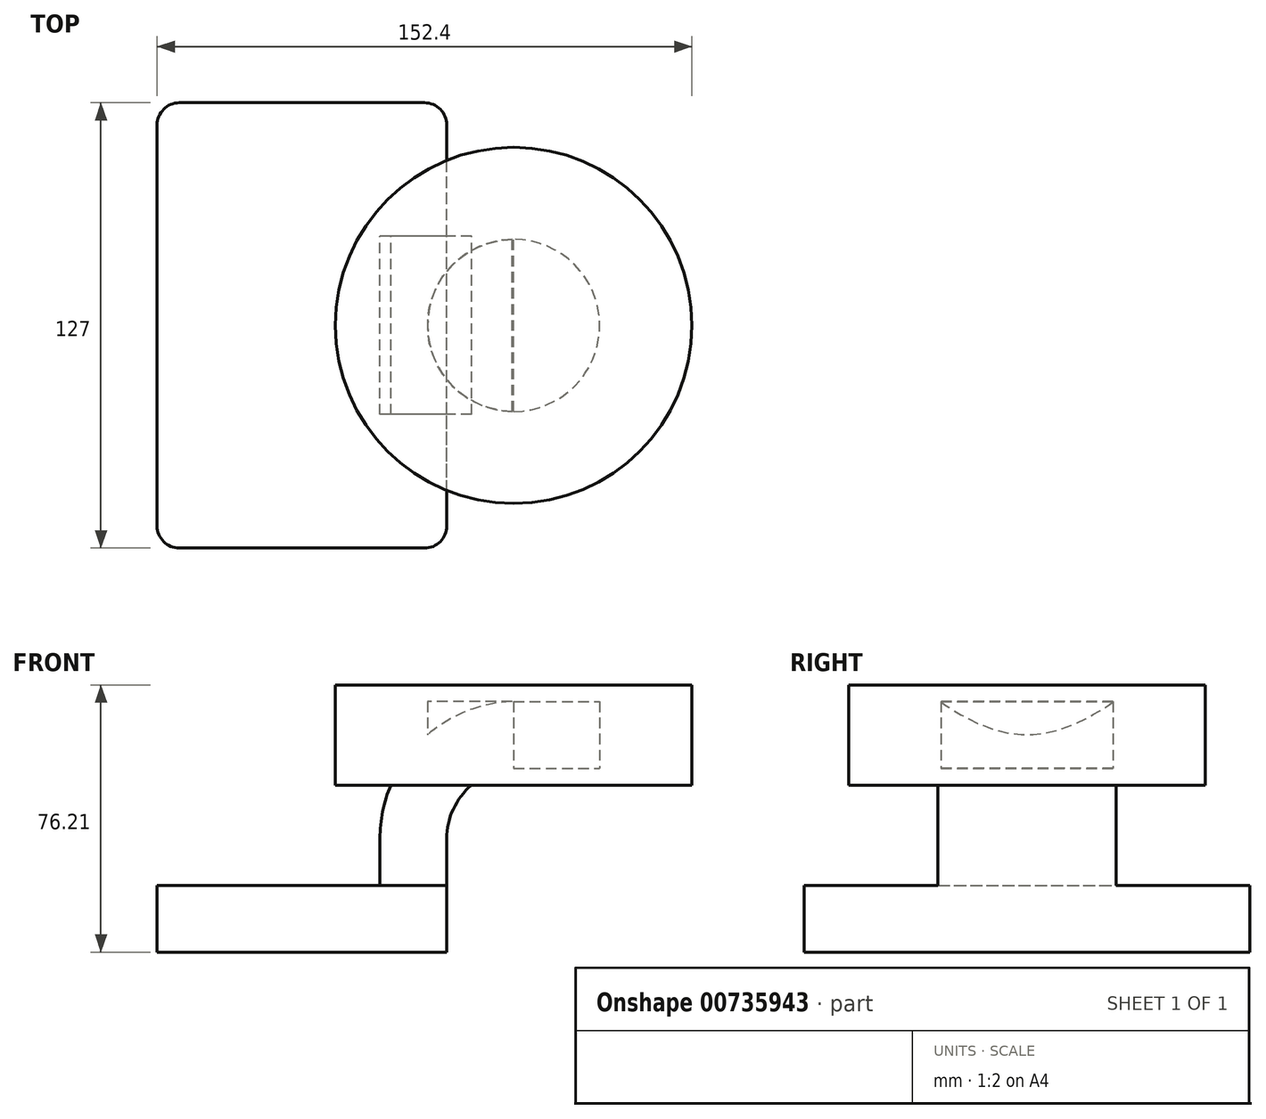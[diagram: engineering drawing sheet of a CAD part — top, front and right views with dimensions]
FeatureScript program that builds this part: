
annotation { "Feature Type Name" : "Feature", "Feature Type Description" : "" }
export const myFeature = defineFeature(function(context is Context, id is Id, definition is map)
    precondition{}
    {
        {
            var Q0;
            Q0=qCreatedBy(makeId("Front.planeOp"),FACE);
            var sketch = newSketch(context, id + "F0", { "sketchPlane" : qUnion([Q0])});
            skLineSegment(sketch, "E0.bottom", {"start": v(41.28, -9.53) * mm, "end": v(-41.28, -9.53) * mm});
            skLineSegment(sketch, "E0.top", {"start": v(41.27, 9.53) * mm, "end": v(-41.28, 9.52) * mm});
            skLineSegment(sketch, "E0.left", {"start": v(41.28, -9.53) * mm, "end": v(41.28, 9.53) * mm});
            skLineSegment(sketch, "E0.right", {"start": v(-41.28, -9.53) * mm, "end": v(-41.28, 9.52) * mm});
            skPoint(sketch, "E0.middle", {"position": v(0, 0) * mm});
            skLineSegment(sketch, "E1.bottom", {"start": v(111.13, 38.1) * mm, "end": v(60.33, 38.1) * mm});
            skLineSegment(sketch, "E1.top", {"start": v(111.13, 66.67) * mm, "end": v(60.33, 66.67) * mm});
            skLineSegment(sketch, "E1.left", {"start": v(111.13, 38.1) * mm, "end": v(111.13, 66.68) * mm});
            skLineSegment(sketch, "E1.right", {"start": v(60.33, 38.1) * mm, "end": v(60.33, 66.68) * mm});
            skPoint(sketch, "E1.middle", {"position": v(85.73, 52.39) * mm});
            skLineSegment(sketch, "E2", {"start": v(41.27, 9.53) * mm, "end": v(41.27, 22.81) * mm});
            skArc(sketch, "E3", {"start": v(41.28, 22.81) * mm, "mid": v(46.8, 36.64) * mm, "end": v(60.33, 42.88) * mm});
            skLineSegment(sketch, "E4", {"start": v(60.33, 42.88) * mm, "end": v(84.86, 42.88) * mm});
            skLineSegment(sketch, "E5.0", {"start": v(59.91, 61.93) * mm, "end": v(84.86, 61.93) * mm});
            skArc(sketch, "E5.1", {"start": v(22.23, 22.81) * mm, "mid": v(33.18, 49.97) * mm, "end": v(59.91, 61.93) * mm});
            skLineSegment(sketch, "E5.2", {"start": v(22.23, 9.53) * mm, "end": v(22.23, 22.81) * mm});
            skLineSegment(sketch, "E6", {"start": v(84.86, 42.88) * mm, "end": v(84.86, 61.93) * mm});
            skFitSpline(sketch, "E7", {"points": [v(-41.28, 9.52) * mm, v(59.91, 61.93) * mm], "startDerivative": vector(47.33, 115.64) * mm, "endDerivative": vector(112.02, -9.85) * mm});
            skSolve(sketch);
        }
        {
            var Q0;
            Q0=makeQuery(id+"F0.imprint","IMPRINT",FACE,{"disambiguationData":[TD([[makeQuery(id+"F0.imprint","IMPRINT",EDGE,{"derivedFrom":sQuery(id+"F0.wireOp",EDGE,"E0.bottom")}),-1.0]])]});
            extrude(context, id + "F1", {"entities" : qUnion([Q0]), "endBound" : BoundingType.SYMMETRIC, "depth" : 127 * mm, "offsetDistance" : 25.4 * mm});
        }
        {
            var Q0;
            {var subQ1=sQuery(id+"F0.wireOp",EDGE,"E2");Q0=makeQuery(id+"F0.imprint","IMPRINT",FACE,{"disambiguationData":[TD([[makeQuery(id+"F0.imprint","IMPRINT",EDGE,{"derivedFrom":subQ1}),1.0]])]});}
            extrude(context, id + "F2", {"entities" : qUnion([Q0]), "operationType" : NewBodyOperationType.ADD, "endBound" : BoundingType.SYMMETRIC, "depth" : 50.8 * mm, "offsetDistance" : 25.4 * mm});
        }
        {
            var Q0;
            Q0=makeQuery(id+"F0.imprint","IMPRINT",FACE,{"disambiguationData":[TD([[makeQuery(id+"F0.imprint","IMPRINT",EDGE,{"derivedFrom":sQuery(id+"F0.wireOp",EDGE,"E5.1")}),1.0]])]});
            extrude(context, id + "F3", {"entities" : qUnion([Q0]), "operationType" : NewBodyOperationType.ADD, "endBound" : BoundingType.SYMMETRIC, "depth" : 15.88 * mm, "offsetDistance" : 25.4 * mm});
        }
        {
            var Q0;
            {var subQ1=sQuery(id+"F0.wireOp",EDGE,"E1.bottom");Q0=makeQuery(id+"F0.imprint","IMPRINT",FACE,{"disambiguationData":[TD([[makeQuery(id+"F0.imprint","IMPRINT",EDGE,{"derivedFrom":subQ1}),-1.0]])]});}
            var Q1;
            Q1=sQuery(id+"F0.wireOp",EDGE,"E1.right");
            revolve(context, id + "F4", {"operationType" : NewBodyOperationType.ADD, "surfaceOperationType" : NewSurfaceOperationType.NEW, "entities" : qUnion([Q0]), "axis" : qUnion([Q1]), "revolveType" : RevolveType.FULL});
        }
        {
            var Q0;
            Q0=makeQuery(id+"F1.opExtrude","CAP_EDGE",EDGE,{"disambiguationData":[OSD([sQuery(id+"F0.wireOp",EDGE,"E0.right")])],"isStart":false});
            var Q1;
            Q1=makeQuery(id+"F1.opExtrude","CAP_EDGE",EDGE,{"disambiguationData":[OSD([sQuery(id+"F0.wireOp",EDGE,"E0.left")])],"isStart":false});
            var Q2;
            Q2=makeQuery(id+"F1.opExtrude","CAP_EDGE",EDGE,{"disambiguationData":[OSD([sQuery(id+"F0.wireOp",EDGE,"E0.right")])],"isStart":true});
            var Q3;
            Q3=makeQuery(id+"F1.opExtrude","CAP_EDGE",EDGE,{"disambiguationData":[OSD([sQuery(id+"F0.wireOp",EDGE,"E0.left")])],"isStart":true});
            fillet(context, id + "F5", {"entities" : qUnion([Q0, Q1, Q2, Q3]), "radius" : 6.35 * mm, "tangentPropagation" : true, "allowEdgeOverflow" : false});
        }
    });
